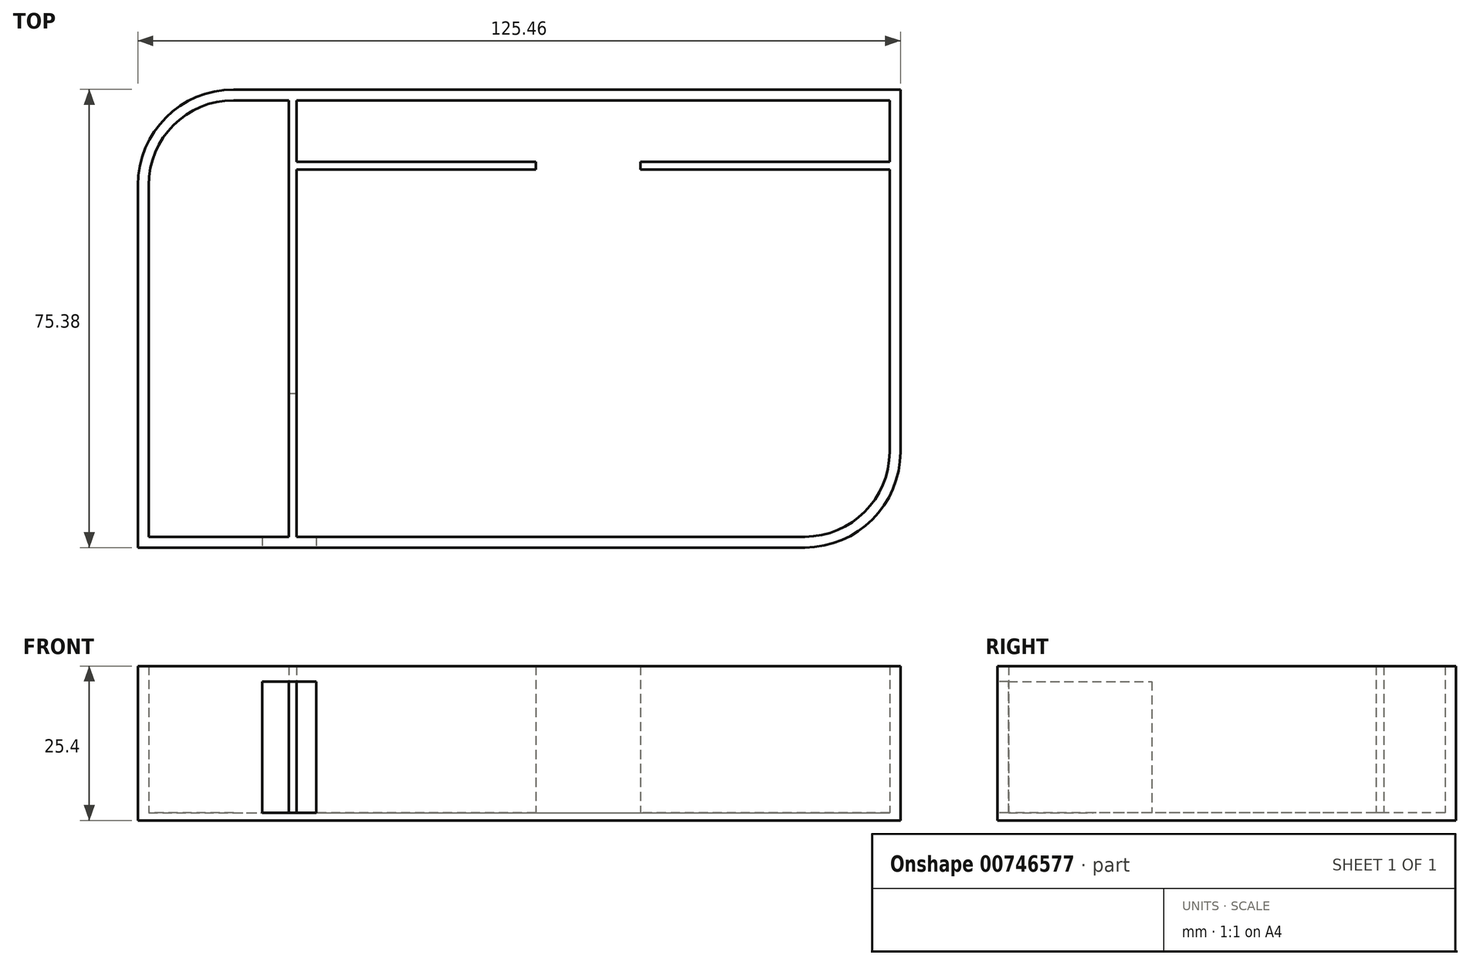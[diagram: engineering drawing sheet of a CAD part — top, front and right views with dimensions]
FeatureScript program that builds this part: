
annotation { "Feature Type Name" : "Feature", "Feature Type Description" : "" }
export const myFeature = defineFeature(function(context is Context, id is Id, definition is map)
    precondition{}
    {
        {
            var Q0;
            Q0=qCreatedBy(makeId("Top.planeOp"),FACE);
            var sketch = newSketch(context, id + "F0", { "sketchPlane" : qUnion([Q0])});
            skLineSegment(sketch, "E0.bottom", {"start": v(-49.75, 44.05) * mm, "end": v(-40.67, 44.05) * mm});
            skLineSegment(sketch, "E0.top", {"start": v(-63.72, -27.77) * mm, "end": v(-40.67, -27.77) * mm});
            skLineSegment(sketch, "E0.left", {"start": v(-63.72, 30.08) * mm, "end": v(-63.72, -27.77) * mm});
            skLineSegment(sketch, "E0.right", {"start": v(58.18, 44.05) * mm, "end": v(58.18, 33.95) * mm});
            skPoint(sketch, "E1.visualSharp", {"position": v(-63.72, 44.05) * mm});
            skArc(sketch, "E1.filletArc", {"start": v(-49.75, 44.05) * mm, "mid": v(-59.63, 39.96) * mm, "end": v(-63.72, 30.08) * mm});
            skPoint(sketch, "E2.visualSharp", {"position": v(58.18, -27.77) * mm});
            skArc(sketch, "E2.filletArc", {"start": v(44.21, -27.77) * mm, "mid": v(54.1, -23.68) * mm, "end": v(58.18, -13.8) * mm});
            skArc(sketch, "E3.0", {"start": v(-49.75, 45.83) * mm, "mid": v(-60.88, 41.21) * mm, "end": v(-65.5, 30.08) * mm});
            skLineSegment(sketch, "E3.1", {"start": v(-65.5, -29.55) * mm, "end": v(44.21, -29.55) * mm});
            skArc(sketch, "E3.2", {"start": v(44.21, -29.55) * mm, "mid": v(55.35, -24.94) * mm, "end": v(59.96, -13.8) * mm});
            skLineSegment(sketch, "E3.3", {"start": v(-65.5, 30.08) * mm, "end": v(-65.5, -29.55) * mm});
            skLineSegment(sketch, "E3.4", {"start": v(59.96, 45.83) * mm, "end": v(59.96, -13.8) * mm});
            skLineSegment(sketch, "E3.5", {"start": v(-49.75, 45.83) * mm, "end": v(59.96, 45.83) * mm});
            skLineSegment(sketch, "E4.left", {"start": v(-40.67, 44.05) * mm, "end": v(-40.67, -27.77) * mm});
            skLineSegment(sketch, "E4.right", {"start": v(-39.4, 44.05) * mm, "end": v(-39.4, 33.95) * mm});
            skLineSegment(sketch, "E5.bottom", {"start": v(58.18, 32.68) * mm, "end": v(17.17, 32.68) * mm});
            skLineSegment(sketch, "E5.top", {"start": v(58.18, 33.95) * mm, "end": v(17.17, 33.95) * mm});
            skLineSegment(sketch, "E6.left", {"start": v(0, 33.95) * mm, "end": v(0, 32.68) * mm});
            skLineSegment(sketch, "E6.right", {"start": v(17.17, 33.95) * mm, "end": v(17.17, 32.68) * mm});
            skLineSegment(sketch, "E7.trimOffspring", {"start": v(0, 32.68) * mm, "end": v(-39.4, 32.68) * mm});
            skLineSegment(sketch, "E8.trimOffspring", {"start": v(0, 33.95) * mm, "end": v(-39.4, 33.95) * mm});
            skLineSegment(sketch, "E9.trimOffspring", {"start": v(-39.4, 32.68) * mm, "end": v(-39.4, -27.77) * mm});
            skLineSegment(sketch, "E10.trimOffspring", {"start": v(-39.4, 44.05) * mm, "end": v(58.18, 44.05) * mm});
            skLineSegment(sketch, "E11.trimOffspring", {"start": v(58.18, 32.68) * mm, "end": v(58.18, -13.8) * mm});
            skLineSegment(sketch, "E12.trimOffspring", {"start": v(-39.4, -27.77) * mm, "end": v(44.21, -27.77) * mm});
            skSolve(sketch);
        }
        {
            var Q0;
            Q0=makeQuery(id+"F0.imprint","IMPRINT",FACE,{"disambiguationData":[TD([[makeQuery(id+"F0.imprint","IMPRINT",EDGE,{"derivedFrom":sQuery(id+"F0.wireOp",EDGE,"E0.bottom")}),1.0]])]});
            extrude(context, id + "F1", {"entities" : qUnion([Q0]), "depth" : 25.4 * mm, "offsetDistance" : 25.4 * mm});
        }
        {
            var Q0;
            Q0=makeQuery(id+"F0.imprint","IMPRINT",FACE,{"disambiguationData":[TD([[makeQuery(id+"F0.imprint","IMPRINT",EDGE,{"derivedFrom":sQuery(id+"F0.wireOp",EDGE,"E0.bottom")}),-1.0]])]});
            var Q1;
            Q1=makeQuery(id+"F0.imprint","IMPRINT",FACE,{"disambiguationData":[TD([[makeQuery(id+"F0.imprint","IMPRINT",EDGE,{"derivedFrom":sQuery(id+"F0.wireOp",EDGE,"E0.right")}),-1.0]])]});
            extrude(context, id + "F2", {"entities" : qUnion([Q0, Q1]), "operationType" : NewBodyOperationType.ADD, "depth" : 1.27 * mm, "offsetDistance" : 25.4 * mm});
        }
        {
            var Q0;
            Q0=makeQuery(id+"F1.opExtrude","SWEPT_FACE",FACE,{"disambiguationData":[OSD([sQuery(id+"F0.wireOp",EDGE,"E3.1")])]});
            var sketch = newSketch(context, id + "F3", { "sketchPlane" : qUnion([Q0])});
            skLineSegment(sketch, "E13.bottom", {"start": v(-45.02, 22.86) * mm, "end": v(-36.13, 22.86) * mm});
            skLineSegment(sketch, "E13.top", {"start": v(-45.02, 1.27) * mm, "end": v(-36.13, 1.27) * mm});
            skLineSegment(sketch, "E13.left", {"start": v(-45.02, 22.86) * mm, "end": v(-45.02, 1.27) * mm});
            skLineSegment(sketch, "E13.right", {"start": v(-36.13, 22.86) * mm, "end": v(-36.13, 1.27) * mm});
            skSolve(sketch);
        }
        {
            var Q0;
            Q0=makeQuery(id+"F3.imprint","IMPRINT",FACE,{"disambiguationData":[TD([[makeQuery(id+"F3.imprint","IMPRINT",EDGE,{"derivedFrom":sQuery(id+"F3.wireOp",EDGE,"E13.bottom")}),-1.0]])]});
            extrude(context, id + "F4", {"entities" : qUnion([Q0]), "operationType" : NewBodyOperationType.REMOVE, "oppositeDirection" : true, "depth" : 25.4 * mm, "offsetDistance" : 25.4 * mm});
        }
    });
